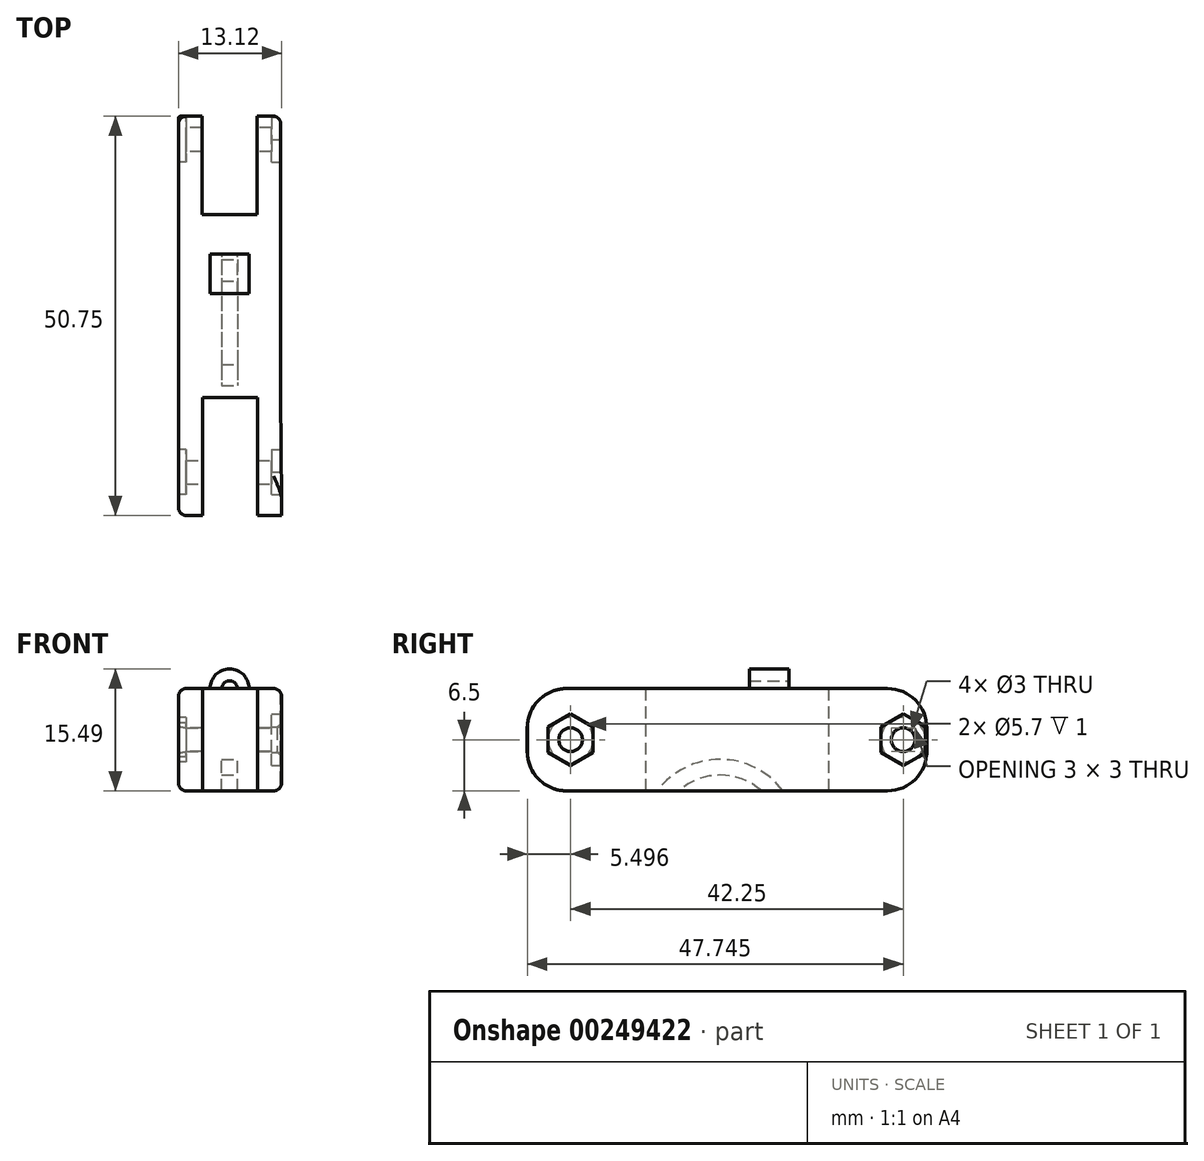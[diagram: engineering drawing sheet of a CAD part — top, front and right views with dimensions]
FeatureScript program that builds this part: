
annotation { "Feature Type Name" : "Feature", "Feature Type Description" : "" }
export const myFeature = defineFeature(function(context is Context, id is Id, definition is map)
    precondition{}
    {
        {
            var Q0;
            Q0=qCreatedBy(makeId("Top.planeOp"),FACE);
            var sketch = newSketch(context, id + "F0", { "sketchPlane" : qUnion([Q0])});
            skLineSegment(sketch, "E0.bottom", {"start": v(-6.5, 7.54) * mm, "end": v(6.5, 7.54) * mm});
            skLineSegment(sketch, "E0.top", {"start": v(-6.5, -15.71) * mm, "end": v(6.5, -15.71) * mm});
            skLineSegment(sketch, "E0.left", {"start": v(-6.5, 7.54) * mm, "end": v(-6.5, -15.71) * mm});
            skLineSegment(sketch, "E0.right", {"start": v(6.5, 7.54) * mm, "end": v(6.5, -15.71) * mm});
            skLineSegment(sketch, "E1", {"start": v(-6.5, 7.54) * mm, "end": v(-6.5, 20.04) * mm});
            skLineSegment(sketch, "E2", {"start": v(-6.5, 20.04) * mm, "end": v(-3.5, 20.04) * mm});
            skLineSegment(sketch, "E3", {"start": v(-3.5, 20.04) * mm, "end": v(-3.5, 7.54) * mm});
            skPoint(sketch, "E3.endSnap0", {"position": v(0, 7.54) * mm});
            skLineSegment(sketch, "E4", {"start": v(-3.5, 7.54) * mm, "end": v(3.5, 7.54) * mm});
            skLineSegment(sketch, "E5", {"start": v(3.5, 7.54) * mm, "end": v(3.5, 20.04) * mm});
            skLineSegment(sketch, "E6", {"start": v(3.5, 20.04) * mm, "end": v(6.5, 20.04) * mm});
            skLineSegment(sketch, "E7", {"start": v(6.5, 20.04) * mm, "end": v(6.5, 7.54) * mm});
            skLineSegment(sketch, "E8", {"start": v(-6.5, -15.71) * mm, "end": v(-6.5, -30.71) * mm});
            skLineSegment(sketch, "E9", {"start": v(-6.5, -30.71) * mm, "end": v(-3.44, -30.71) * mm});
            skLineSegment(sketch, "E10", {"start": v(-3.44, -30.71) * mm, "end": v(-3.44, -15.71) * mm});
            skLineSegment(sketch, "E11", {"start": v(-3.44, -15.71) * mm, "end": v(3.56, -15.71) * mm});
            skLineSegment(sketch, "E12", {"start": v(3.56, -15.71) * mm, "end": v(3.56, -30.71) * mm});
            skLineSegment(sketch, "E13", {"start": v(3.56, -30.71) * mm, "end": v(6.62, -30.71) * mm});
            skLineSegment(sketch, "E14", {"start": v(6.62, -30.71) * mm, "end": v(6.5, -15.71) * mm});
            skPoint(sketch, "E15", {"position": v(-6.5, -23.21) * mm});
            skPoint(sketch, "E16", {"position": v(-6.5, 13.79) * mm});
            skSolve(sketch);
        }
        {
            var Q0;
            {var subQ3=sQuery(id+"F0.wireOp",EDGE,"E0.left");Q0=makeQuery(id+"F0.imprint","IMPRINT",FACE,{"disambiguationData":[TD([[makeQuery(id+"F0.imprint","IMPRINT",EDGE,{"derivedFrom":subQ3}),1.0]])]});}
            var Q1;
            {var subQ0=sQuery(id+"F0.wireOp",EDGE,"E1");Q1=makeQuery(id+"F0.imprint","IMPRINT",FACE,{"disambiguationData":[TD([[makeQuery(id+"F0.imprint","IMPRINT",EDGE,{"derivedFrom":subQ0}),-1.0]])]});}
            var Q2;
            {var subQ2=sQuery(id+"F0.wireOp",EDGE,"E5");Q2=makeQuery(id+"F0.imprint","IMPRINT",FACE,{"disambiguationData":[TD([[makeQuery(id+"F0.imprint","IMPRINT",EDGE,{"derivedFrom":subQ2}),-1.0]])]});}
            var Q3;
            {var subQ0=sQuery(id+"F0.wireOp",EDGE,"E8");Q3=makeQuery(id+"F0.imprint","IMPRINT",FACE,{"disambiguationData":[TD([[makeQuery(id+"F0.imprint","IMPRINT",EDGE,{"derivedFrom":subQ0}),1.0]])]});}
            var Q4;
            {var subQ2=sQuery(id+"F0.wireOp",EDGE,"E12");Q4=makeQuery(id+"F0.imprint","IMPRINT",FACE,{"disambiguationData":[TD([[makeQuery(id+"F0.imprint","IMPRINT",EDGE,{"derivedFrom":subQ2}),1.0]])]});}
            extrude(context, id + "F1", {"entities" : qUnion([Q0, Q1, Q2, Q3, Q4]), "depth" : 13 * mm});
        }
        {
            var Q0;
            Q0=makeQuery(id+"F1.opExtrude","CAP_EDGE",EDGE,{"disambiguationData":[OSD([sQuery(id+"F0.wireOp",EDGE,"E13")])],"isStart":true});
            var Q1;
            Q1=makeQuery(id+"F1.opExtrude","CAP_EDGE",EDGE,{"disambiguationData":[OSD([sQuery(id+"F0.wireOp",EDGE,"E13")])],"isStart":false});
            var Q2;
            Q2=makeQuery(id+"F1.opExtrude","CAP_EDGE",EDGE,{"disambiguationData":[OSD([sQuery(id+"F0.wireOp",EDGE,"E9")])],"isStart":false});
            var Q3;
            Q3=makeQuery(id+"F1.opExtrude","CAP_EDGE",EDGE,{"disambiguationData":[OSD([sQuery(id+"F0.wireOp",EDGE,"E9")])],"isStart":true});
            var Q4;
            Q4=makeQuery(id+"F1.opExtrude","CAP_EDGE",EDGE,{"disambiguationData":[OSD([sQuery(id+"F0.wireOp",EDGE,"E2")])],"isStart":false});
            var Q5;
            Q5=makeQuery(id+"F1.opExtrude","CAP_EDGE",EDGE,{"disambiguationData":[OSD([sQuery(id+"F0.wireOp",EDGE,"E2")])],"isStart":true});
            var Q6;
            Q6=makeQuery(id+"F1.opExtrude","CAP_EDGE",EDGE,{"disambiguationData":[OSD([sQuery(id+"F0.wireOp",EDGE,"E6")])],"isStart":false});
            var Q7;
            Q7=makeQuery(id+"F1.opExtrude","CAP_EDGE",EDGE,{"disambiguationData":[OSD([sQuery(id+"F0.wireOp",EDGE,"E6")])],"isStart":true});
            fillet(context, id + "F2", {"entities" : qUnion([Q0, Q1, Q2, Q3, Q4, Q5, Q6, Q7]), "radius" : 5 * mm, "tangentPropagation" : true, "allowEdgeOverflow" : false});
        }
        {
            var Q0;
            Q0=qCreatedBy(makeId("Right.planeOp"),FACE);
            var sketch = newSketch(context, id + "F3", { "sketchPlane" : qUnion([Q0])});
            skPoint(sketch, "E17", {"position": v(20.54, 6.5) * mm});
            skPoint(sketch, "E18", {"position": v(17.04, 0.13) * mm});
            skCircle(sketch, "E19", {"center": v(17.04, 6.5) * mm, "radius": 1.5 * mm});
            skCircle(sketch, "E20.MirrorC", {"center": v(-25.21, 6.5) * mm, "radius": 1.5 * mm});
            skPoint(sketch, "E21.orphan", {"position": v(20.54, 0.13) * mm});
            skPoint(sketch, "E22.0.2.start.orphan", {"position": v(13.54, 0.13) * mm});
            skPoint(sketch, "E22.0.3.end.orphan", {"position": v(20.54, 12.87) * mm});
            skPoint(sketch, "E22.0.3.start.orphan", {"position": v(14.29, 12.87) * mm});
            skPoint(sketch, "E23", {"position": v(0, 13.07) * mm});
            skSolve(sketch);
        }
        {
            var Q0;
            Q0=makeQuery(id+"F3.imprint","IMPRINT",FACE,{"disambiguationData":[TD([[makeQuery(id+"F3.imprint","IMPRINT",EDGE,{"derivedFrom":sQuery(id+"F3.wireOp",EDGE,"E19")}),1.0]])]});
            var Q1;
            Q1=makeQuery(id+"F3.imprint","IMPRINT",FACE,{"disambiguationData":[TD([[makeQuery(id+"F3.imprint","IMPRINT",EDGE,{"derivedFrom":sQuery(id+"F3.wireOp",EDGE,"E20.MirrorC")}),-1.0]])]});
            var Q2;
            Q2=sQuery(id+"F3.wireOp",EDGE,"E19");
            extrude(context, id + "F4", {"entities" : qUnion([Q0, Q1]), "operationType" : NewBodyOperationType.REMOVE, "surfaceEntities" : qUnion([Q2]), "depth" : 54 * mm, "symmetric" : true});
        }
        {
            var Q0;
            Q0 = qSketchRegion(id + "F3", true);
            extrude(context, id + "F5", {"entities" : qUnion([Q0]), "operationType" : NewBodyOperationType.REMOVE, "oppositeDirection" : true, "depth" : 25 * mm, "symmetric" : true});
        }
        {
            var Q0;
            Q0=makeQuery(id+"F1.opExtrude","SWEPT_FACE",FACE,{"disambiguationData":[OSD([sQuery(id+"F0.wireOp",EDGE,"E0.left"),sQuery(id+"F0.wireOp",EDGE,"E1"),sQuery(id+"F0.wireOp",EDGE,"E8")])]});
            var sketch = newSketch(context, id + "F6", { "sketchPlane" : qUnion([Q0])});
            skCircle(sketch, "E24", {"center": v(25.21, 6.5) * mm, "radius": 2.85 * mm});
            skCircle(sketch, "E25", {"center": v(-17.04, 6.5) * mm, "radius": 2.85 * mm});
            skSolve(sketch);
        }
        {
            var Q0;
            Q0 = qSketchRegion(id + "F6", true);
            extrude(context, id + "F7", {"entities" : qUnion([Q0]), "operationType" : NewBodyOperationType.REMOVE, "oppositeDirection" : true, "depth" : 1 * mm});
        }
        {
            var Q0;
            Q0=makeQuery(id+"F1.opExtrude","SWEPT_FACE",FACE,{"disambiguationData":[OSD([sQuery(id+"F0.wireOp",EDGE,"E0.right"),sQuery(id+"F0.wireOp",EDGE,"E7"),sQuery(id+"F0.wireOp",EDGE,"E14")])]});
            var sketch = newSketch(context, id + "F8", { "sketchPlane" : qUnion([Q0])});
            skCircle(sketch, "E26.cCircle", {"center": v(-25.21, 6.5) * mm, "radius": 2.85 * mm, "construction": true});
            skLineSegment(sketch, "E26.0", {"start": v(-28.06, 8.15) * mm, "end": v(-25.21, 9.8) * mm});
            skLineSegment(sketch, "E26.1", {"start": v(-25.21, 9.8) * mm, "end": v(-22.36, 8.15) * mm});
            skLineSegment(sketch, "E26.2", {"start": v(-22.36, 8.15) * mm, "end": v(-22.36, 4.85) * mm});
            skLineSegment(sketch, "E26.3", {"start": v(-22.36, 4.85) * mm, "end": v(-25.21, 3.2) * mm});
            skLineSegment(sketch, "E26.4", {"start": v(-25.21, 3.2) * mm, "end": v(-28.06, 4.85) * mm});
            skLineSegment(sketch, "E26.5", {"start": v(-28.06, 4.85) * mm, "end": v(-28.06, 8.15) * mm});
            skPoint(sketch, "E26.0.midPoint", {"position": v(-26.64, 8.97) * mm});
            skCircle(sketch, "E27.cCircle", {"center": v(17.04, 6.5) * mm, "radius": 2.85 * mm, "construction": true});
            skLineSegment(sketch, "E27.0", {"start": v(14.19, 8.15) * mm, "end": v(17.04, 9.8) * mm});
            skLineSegment(sketch, "E27.1", {"start": v(17.04, 9.8) * mm, "end": v(19.89, 8.15) * mm});
            skLineSegment(sketch, "E27.2", {"start": v(19.89, 8.15) * mm, "end": v(19.89, 4.85) * mm});
            skLineSegment(sketch, "E27.3", {"start": v(19.89, 4.85) * mm, "end": v(17.04, 3.2) * mm});
            skLineSegment(sketch, "E27.4", {"start": v(17.04, 3.2) * mm, "end": v(14.19, 4.85) * mm});
            skLineSegment(sketch, "E27.5", {"start": v(14.19, 4.85) * mm, "end": v(14.19, 8.15) * mm});
            skPoint(sketch, "E27.0.midPoint", {"position": v(15.61, 8.97) * mm});
            skSolve(sketch);
        }
        {
            var Q0;
            Q0=makeQuery(id+"F8.imprint","IMPRINT",FACE,{"disambiguationData":[TD([[makeQuery(id+"F8.imprint","IMPRINT",EDGE,{"derivedFrom":sQuery(id+"F8.wireOp",EDGE,"E26.0")}),-1.0]])]});
            var Q1;
            Q1=makeQuery(id+"F8.imprint","IMPRINT",FACE,{"disambiguationData":[TD([[makeQuery(id+"F8.imprint","IMPRINT",EDGE,{"derivedFrom":sQuery(id+"F8.wireOp",EDGE,"E27.0")}),-1.0]])]});
            extrude(context, id + "F9", {"entities" : qUnion([Q0, Q1]), "operationType" : NewBodyOperationType.REMOVE, "oppositeDirection" : true, "depth" : 1.2 * mm});
        }
        {
            var Q0;
            Q0 = qSketchRegion(id + "F6", true);
            extrude(context, id + "F10", {"entities" : qUnion([Q0]), "operationType" : NewBodyOperationType.REMOVE, "oppositeDirection" : true, "depth" : 1 * mm});
        }
        {
            var Q0;
            Q0 = qSketchRegion(id + "F8", true);
            extrude(context, id + "F11", {"entities" : qUnion([Q0]), "operationType" : NewBodyOperationType.REMOVE, "oppositeDirection" : true, "depth" : 1 * mm});
        }
        {
            var Q0;
            Q0=makeQuery(id+"F1.opExtrude","CAP_EDGE",EDGE,{"disambiguationData":[OSD([sQuery(id+"F0.wireOp",EDGE,"E0.left"),sQuery(id+"F0.wireOp",EDGE,"E1"),sQuery(id+"F0.wireOp",EDGE,"E8")])],"isStart":true});
            var Q1;
            Q1=makeQuery(id+"F1.opExtrude","CAP_EDGE",EDGE,{"disambiguationData":[OSD([sQuery(id+"F0.wireOp",EDGE,"E0.right"),sQuery(id+"F0.wireOp",EDGE,"E7"),sQuery(id+"F0.wireOp",EDGE,"E14")])],"isStart":true});
            fillet(context, id + "F12", {"entities" : qUnion([Q0, Q1]), "radius" : 1 * mm, "tangentPropagation" : true, "allowEdgeOverflow" : false});
        }
        {
            var Q0;
            Q0=qCreatedBy(makeId("Front.planeOp"),FACE);
            var sketch = newSketch(context, id + "F13", { "sketchPlane" : qUnion([Q0])});
            skArc(sketch, "E28", {"start": v(0.99, 13) * mm, "mid": v(0, 13.99) * mm, "end": v(-0.99, 13) * mm});
            skArc(sketch, "E29", {"start": v(2.49, 13) * mm, "mid": v(0, 15.49) * mm, "end": v(-2.49, 13) * mm});
            skLineSegment(sketch, "E30", {"start": v(-2.49, 13) * mm, "end": v(-0.99, 13) * mm});
            skLineSegment(sketch, "E31", {"start": v(0.99, 13) * mm, "end": v(2.49, 13) * mm});
            skArc(sketch, "E32", {"start": v(-2.49, 0) * mm, "mid": v(0, -4.1) * mm, "end": v(2.49, 0) * mm});
            skArc(sketch, "E33", {"start": v(-0.99, 0) * mm, "mid": v(0, -0.98) * mm, "end": v(0.99, 0) * mm});
            skLineSegment(sketch, "E34", {"start": v(0.99, 0) * mm, "end": v(2.49, 0) * mm});
            skLineSegment(sketch, "E35", {"start": v(-0.99, 0) * mm, "end": v(-2.49, 0) * mm});
            skSolve(sketch);
        }
        {
            var Q0;
            Q0=makeQuery(id+"F13.imprint","IMPRINT",FACE,{"disambiguationData":[TD([[makeQuery(id+"F13.imprint","IMPRINT",EDGE,{"derivedFrom":sQuery(id+"F13.wireOp",EDGE,"E28")}),-1.0]])]});
            var Q1;
            Q1=makeQuery(id+"F13.imprint","IMPRINT",FACE,{"disambiguationData":[TD([[makeQuery(id+"F13.imprint","IMPRINT",EDGE,{"derivedFrom":sQuery(id+"F13.wireOp",EDGE,"E32")}),1.0]])]});
            extrude(context, id + "F14", {"entities" : qUnion([Q0, Q1]), "operationType" : NewBodyOperationType.ADD, "depth" : 5 * mm, "symmetric" : true});
        }
        {
            var Q0;
            Q0=makeQuery(id+"F8.imprint","IMPRINT",FACE,{"disambiguationData":[TD([[makeQuery(id+"F8.imprint","IMPRINT",EDGE,{"derivedFrom":sQuery(id+"F8.wireOp",EDGE,"E26.0")}),-1.0]])]});
            extrude(context, id + "F15", {"entities" : qUnion([Q0]), "operationType" : NewBodyOperationType.REMOVE, "depth" : 1.2 * mm});
        }
        {
            var Q0;
            Q0=makeQuery(id+"F14.opExtrude","CAP_FACE",FACE,{"disambiguationData":[OSD([sQuery(id+"F13.wireOp",EDGE,"E32"),sQuery(id+"F13.wireOp",EDGE,"E33"),sQuery(id+"F13.wireOp",EDGE,"E34"),sQuery(id+"F13.wireOp",EDGE,"E35")])],"isStart":true});
            var sketch = newSketch(context, id + "F16", { "sketchPlane" : qUnion([Q0])});
            skArc(sketch, "E36.0", {"start": v(2.49, 0) * mm, "mid": v(0, -4.1) * mm, "end": v(-2.49, 0) * mm});
            skArc(sketch, "E37.0.0", {"start": v(0.99, 0) * mm, "mid": v(0, -0.98) * mm, "end": v(-0.99, 0) * mm});
            skLineSegment(sketch, "E37.0.1", {"start": v(-0.99, 0) * mm, "end": v(-2.49, 0) * mm});
            skArc(sketch, "E37.0.2", {"start": v(-2.49, 0) * mm, "mid": v(0, -4.1) * mm, "end": v(2.49, 0) * mm});
            skLineSegment(sketch, "E37.0.3", {"start": v(2.49, 0) * mm, "end": v(0.99, 0) * mm});
            skSolve(sketch);
        }
        {
            var Q0;
            Q0=makeQuery(id+"F16.imprint","IMPRINT",FACE,{"disambiguationData":[TD([[makeQuery(id+"F16.imprint","IMPRINT",EDGE,{"derivedFrom":sQuery(id+"F16.wireOp",EDGE,"E37.0.0")}),1.0]])]});
            extrude(context, id + "F17", {"entities" : qUnion([Q0]), "operationType" : NewBodyOperationType.REMOVE, "endBound" : BoundingType.THROUGH_ALL, "oppositeDirection" : true, "depth" : 25 * mm});
        }
        {
            var Q0;
            Q0=qCreatedBy(makeId("Right.planeOp"),FACE);
            var sketch = newSketch(context, id + "F18", { "sketchPlane" : qUnion([Q0])});
            skArc(sketch, "E38", {"start": v(1.78, 0) * mm, "mid": v(-6.22, 4) * mm, "end": v(-14.22, 0) * mm});
            skArc(sketch, "E39", {"start": v(-0.93, 0) * mm, "mid": v(-6.22, 2) * mm, "end": v(-11.51, 0) * mm});
            skLineSegment(sketch, "E40", {"start": v(1.78, 0) * mm, "end": v(-0.93, 0) * mm});
            skLineSegment(sketch, "E41.trimOffspring", {"start": v(-11.51, 0) * mm, "end": v(-14.22, 0) * mm});
            skPoint(sketch, "E42.orphan", {"position": v(7.54, 0) * mm});
            skPoint(sketch, "E43.orphan", {"position": v(-15.71, 0) * mm});
            skSolve(sketch);
        }
        {
            var Q0;
            Q0 = qSketchRegion(id + "F18", true);
            extrude(context, id + "F19", {"entities" : qUnion([Q0]), "operationType" : NewBodyOperationType.REMOVE, "oppositeDirection" : true, "depth" : 2 * mm, "symmetric" : true});
        }
    });
